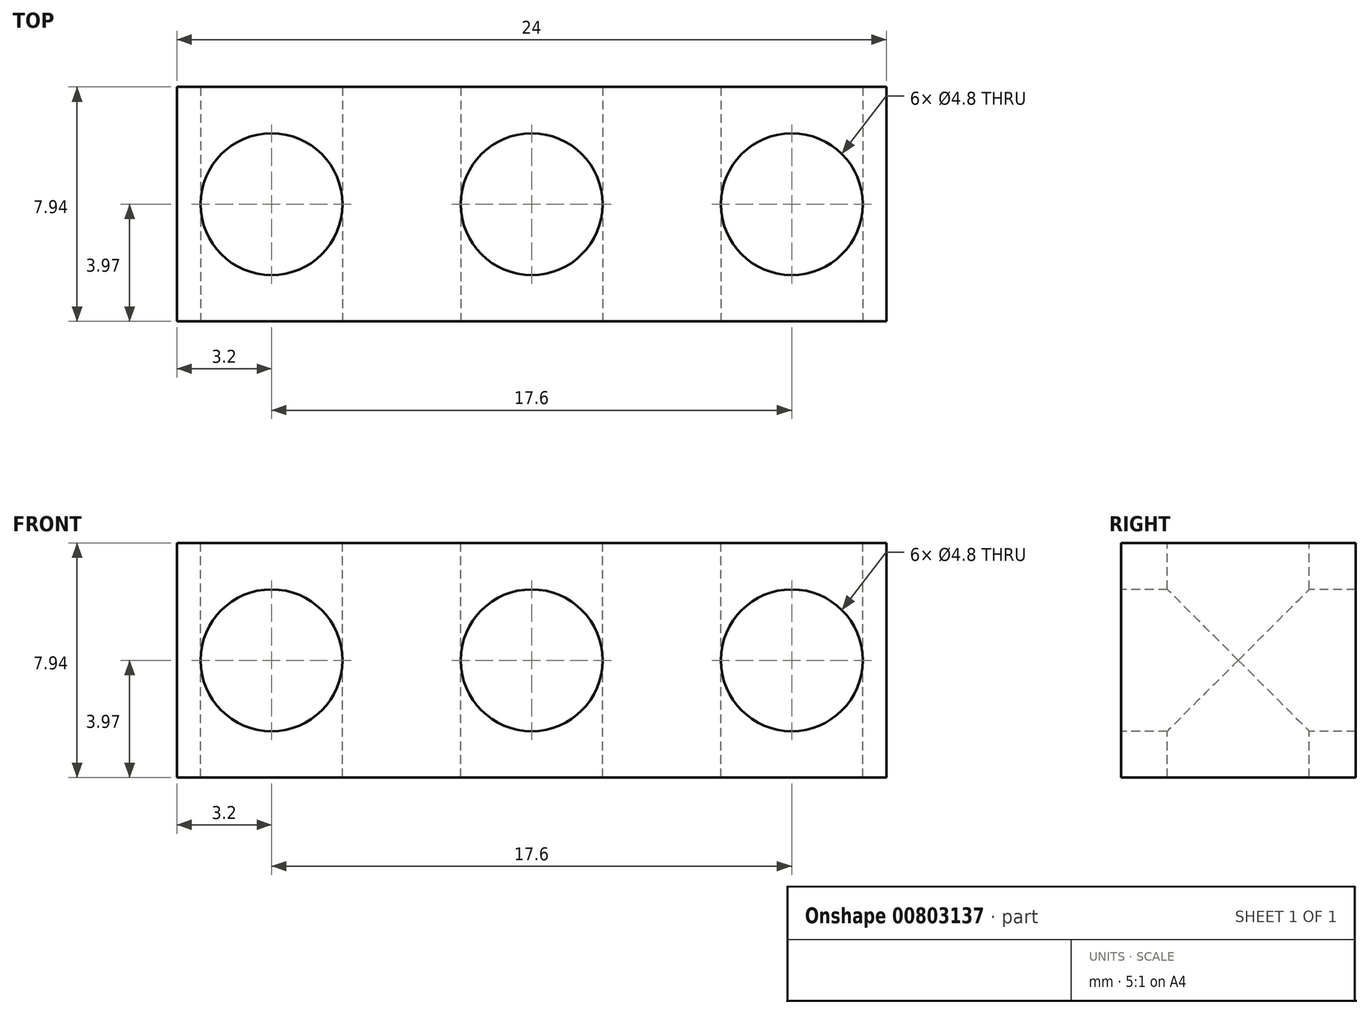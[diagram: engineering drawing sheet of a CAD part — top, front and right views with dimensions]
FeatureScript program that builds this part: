
annotation { "Feature Type Name" : "Feature", "Feature Type Description" : "" }
export const myFeature = defineFeature(function(context is Context, id is Id, definition is map)
    precondition{}
    {
        {
            var Q0;
            Q0=qCreatedBy(makeId("Top.planeOp"),FACE);
            var sketch = newSketch(context, id + "F0", { "sketchPlane" : qUnion([Q0])});
            skLineSegment(sketch, "E0.bottom", {"start": v(12, -3.97) * mm, "end": v(-12, -3.97) * mm});
            skLineSegment(sketch, "E0.top", {"start": v(12, 3.97) * mm, "end": v(-12, 3.97) * mm});
            skLineSegment(sketch, "E0.left", {"start": v(12, -3.97) * mm, "end": v(12, 3.97) * mm});
            skLineSegment(sketch, "E0.right", {"start": v(-12, -3.97) * mm, "end": v(-12, 3.97) * mm});
            skPoint(sketch, "E0.middle", {"position": v(0, 0) * mm});
            skSolve(sketch);
        }
        {
            var Q0;
            Q0 = qSketchRegion(id + "F0", true);
            extrude(context, id + "F1", {"entities" : qUnion([Q0]), "endBound" : BoundingType.SYMMETRIC, "depth" : 7.94 * mm, "offsetDistance" : 25 * mm});
        }
        {
            var Q0;
            Q0=makeQuery(id+"F1.opExtrude","CAP_FACE",FACE,{"disambiguationData":[OSD([sQuery(id+"F0.wireOp",EDGE,"E0.bottom"),sQuery(id+"F0.wireOp",EDGE,"E0.top"),sQuery(id+"F0.wireOp",EDGE,"E0.left"),sQuery(id+"F0.wireOp",EDGE,"E0.right")])],"isStart":false});
            var sketch = newSketch(context, id + "F2", { "sketchPlane" : qUnion([Q0])});
            skCircle(sketch, "E1", {"center": v(0, 0) * mm, "radius": 2.4 * mm});
            skCircle(sketch, "E2", {"center": v(8.8, 0) * mm, "radius": 2.4 * mm});
            skCircle(sketch, "E3", {"center": v(-8.8, 0) * mm, "radius": 2.4 * mm});
            skSolve(sketch);
        }
        {
            var Q0;
            Q0 = qSketchRegion(id + "F2", true);
            extrude(context, id + "F3", {"entities" : qUnion([Q0]), "operationType" : NewBodyOperationType.REMOVE, "endBound" : BoundingType.THROUGH_ALL, "oppositeDirection" : true, "depth" : 25 * mm, "offsetDistance" : 25 * mm});
        }
        {
            var Q0;
            Q0=makeQuery(id+"F1.opExtrude","SWEPT_FACE",FACE,{"disambiguationData":[OSD([sQuery(id+"F0.wireOp",EDGE,"E0.bottom")])]});
            var sketch = newSketch(context, id + "F4", { "sketchPlane" : qUnion([Q0])});
            skCircle(sketch, "E4", {"center": v(0, 0) * mm, "radius": 2.4 * mm});
            skCircle(sketch, "E5", {"center": v(8.8, 0) * mm, "radius": 2.4 * mm});
            skCircle(sketch, "E6", {"center": v(-8.8, 0) * mm, "radius": 2.4 * mm});
            skSolve(sketch);
        }
        {
            var Q0;
            Q0 = qSketchRegion(id + "F4", true);
            extrude(context, id + "F5", {"entities" : qUnion([Q0]), "operationType" : NewBodyOperationType.REMOVE, "endBound" : BoundingType.THROUGH_ALL, "oppositeDirection" : true, "depth" : 25 * mm, "offsetDistance" : 25 * mm});
        }
    });
